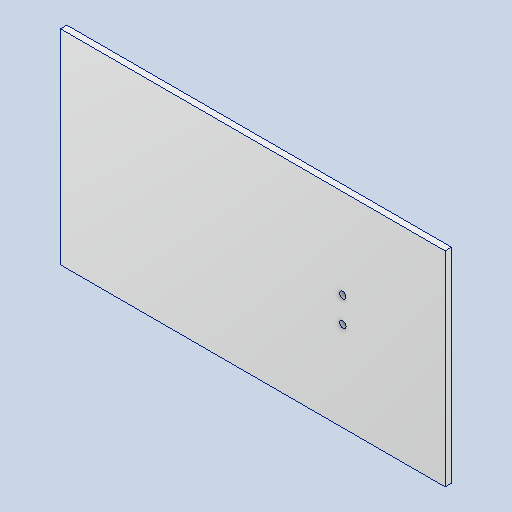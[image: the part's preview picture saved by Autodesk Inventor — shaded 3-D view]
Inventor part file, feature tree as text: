
AUTODESK INVENTOR PART (.ipt)
format: ipt  version: 2023.2 (Build 272271000, 271)  size: 132,608 bytes
history: native  units: mm
features: reference x4, other x4, extrude x2, sketch x2
ambient origin geometry x8: Origin, YZ Plane, XZ Plane, XY Plane, X Axis, Y Axis, Z Axis, Center Point
bodies: Solid1 (feature_tree)
feature tree (12):
  extrude  "Extrusion1"  Depth=5.0mm
  extrude  "Extrusion2"  [1 undecoded]
  sketch  "Sketch1"  dims[d0=5.0mm d1=0.0mm d3=60.0mm]
  reference  "Reference1"
  reference  "Reference2"
  sketch  "Sketch2"  dims[d4=0.0mm d5=0.0mm]
  reference  "Reference3"
  reference  "Reference4"
  parser-record x1  (decoder bookkeeping rows leaked as tree rows — omitted from the tree; the rows remain in map.json)
  other  "Main Assembly.iam"
  other  "V Rail Gantry:1"
  other  "8mm Acme Anti Backlash Nut Block:1"
note: 1 required parameter value undecoded (feature->parameter linkage not recoverable at this tier; creation-order binding heuristic only, values carry confidence <= 0.55)
note: 1 file-system path scrubbed to <path> (originals preserved in map.json)
